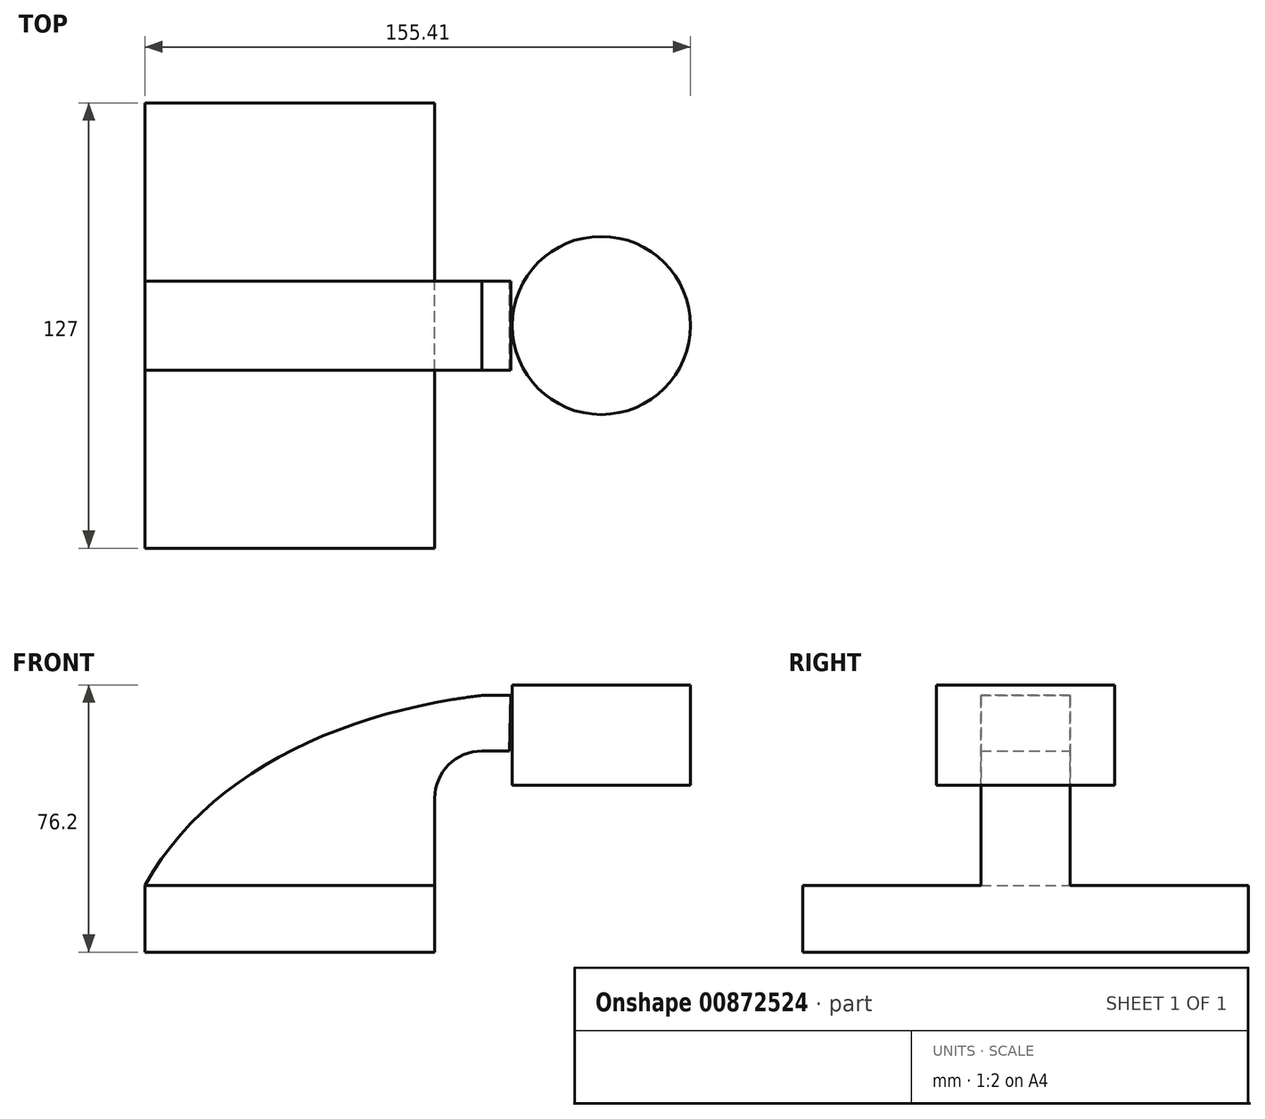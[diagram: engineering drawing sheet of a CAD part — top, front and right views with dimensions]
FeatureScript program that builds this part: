
annotation { "Feature Type Name" : "Feature", "Feature Type Description" : "" }
export const myFeature = defineFeature(function(context is Context, id is Id, definition is map)
    precondition{}
    {
        {
            var Q0;
            Q0=qCreatedBy(makeId("Front.planeOp"),FACE);
            var sketch = newSketch(context, id + "F0", { "sketchPlane" : qUnion([Q0])});
            skLineSegment(sketch, "E0.bottom", {"start": v(-24.58, 32.91) * mm, "end": v(57.97, 32.91) * mm});
            skLineSegment(sketch, "E0.top", {"start": v(-24.58, 13.86) * mm, "end": v(57.97, 13.86) * mm});
            skLineSegment(sketch, "E0.left", {"start": v(-24.58, 32.91) * mm, "end": v(-24.58, 13.86) * mm});
            skLineSegment(sketch, "E0.right", {"start": v(57.97, 32.91) * mm, "end": v(57.97, 13.86) * mm});
            skLineSegment(sketch, "E1.bottom", {"start": v(80.03, 90.06) * mm, "end": v(130.83, 90.06) * mm});
            skLineSegment(sketch, "E1.top", {"start": v(80.03, 61.49) * mm, "end": v(130.83, 61.49) * mm});
            skLineSegment(sketch, "E1.left", {"start": v(80.03, 90.06) * mm, "end": v(80.03, 61.49) * mm});
            skLineSegment(sketch, "E1.right", {"start": v(130.83, 90.06) * mm, "end": v(130.83, 61.49) * mm});
            skLineSegment(sketch, "E2", {"start": v(57.97, 32.91) * mm, "end": v(57.97, 57.73) * mm});
            skArc(sketch, "E3", {"start": v(57.97, 57.73) * mm, "mid": v(61.92, 67.26) * mm, "end": v(71.45, 71.2) * mm});
            skLineSegment(sketch, "E4", {"start": v(71.45, 71.2) * mm, "end": v(79.23, 71.2) * mm});
            skLineSegment(sketch, "E5.0", {"start": v(71.45, 87.08) * mm, "end": v(79.64, 87.08) * mm});
            skArc(sketch, "E5.1", {"start": v(42.1, 57.73) * mm, "mid": v(50.7, 78.48) * mm, "end": v(71.45, 87.08) * mm});
            skLineSegment(sketch, "E5.2", {"start": v(42.1, 33.1) * mm, "end": v(42.1, 57.73) * mm});
            skFitSpline(sketch, "E6", {"points": [v(-24.58, 32.91) * mm, v(71.45, 87.08) * mm], "startDerivative": vector(53.27, 96.4) * mm, "endDerivative": vector(121.22, 14.76) * mm});
            skLineSegment(sketch, "E7", {"start": v(105.43, 61.49) * mm, "end": v(105.43, 90.06) * mm});
            skLineSegment(sketch, "E8", {"start": v(79.64, 87.08) * mm, "end": v(79.23, 71.2) * mm});
            skSolve(sketch);
        }
        {
            var Q0;
            Q0=makeQuery(id+"F0.imprint","IMPRINT",FACE,{"disambiguationData":[TD([[makeQuery(id+"F0.imprint","IMPRINT",EDGE,{"derivedFrom":sQuery(id+"F0.wireOp",EDGE,"E0.bottom")}),-1.0]])]});
            extrude(context, id + "F1", {"entities" : qUnion([Q0]), "endBound" : BoundingType.SYMMETRIC, "depth" : 127 * mm, "offsetDistance" : 25.4 * mm});
        }
        {
            var Q0;
            {var subQ0=sQuery(id+"F0.wireOp",EDGE,"E1.left");var subQ1=sQuery(id+"F0.wireOp",EDGE,"E1.top");var subQ2=makeQuery(id+"F0.imprint","INTERSECT",VERTEX,{"derivedFrom":[subQ1,subQ0]});Q0=makeQuery(id+"F0.imprint","IMPRINT",FACE,{"disambiguationData":[TD([[makeQuery(id+"F0.imprint","IMPRINT",EDGE,{"disambiguationData":[TD([[subQ2,-1.0]])],"derivedFrom":subQ1}),1.0]])]});}
            var Q1;
            Q1=sQuery(id+"F0.wireOp",EDGE,"E7");
            revolve(context, id + "F2", {"surfaceOperationType" : NewSurfaceOperationType.NEW, "entities" : qUnion([Q0]), "axis" : qUnion([Q1]), "revolveType" : RevolveType.FULL});
        }
        {
            var Q0;
            {var subQ0=sQuery(id+"F0.wireOp",EDGE,"E0.bottom");Q0=makeQuery(id+"F0.imprint","IMPRINT",FACE,{"disambiguationData":[TD([[makeQuery(id+"F0.imprint","IMPRINT",EDGE,{"derivedFrom":subQ0}),1.0]])]});}
            extrude(context, id + "F3", {"entities" : qUnion([Q0]), "operationType" : NewBodyOperationType.ADD, "endBound" : BoundingType.SYMMETRIC, "depth" : 25.4 * mm, "offsetDistance" : 25.4 * mm});
        }
    });
